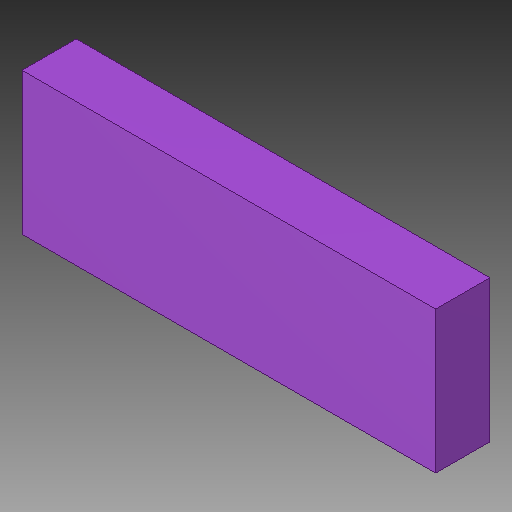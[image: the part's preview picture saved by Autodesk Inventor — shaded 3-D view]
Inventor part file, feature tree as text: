
AUTODESK INVENTOR PART (.ipt)
format: ipt  version: 2019 (Build 230136000, 136)  size: 88,064 bytes
history: native  units: in
note: dims shown in document units (in); Inventor stores cm internally (conversion verified against a paired STEP export)
features: extrude x1, other x1
ambient origin geometry x8: Origin, YZ Plane, XZ Plane, XY Plane, X Axis, Y Axis, Z Axis, Center Point
bodies: Solid1 (feature_tree)
feature tree (2):
  extrude  "Extrusion1"  Depth=0.0394in TaperAngle=0.0deg
  other  "1X03, SIGNALOUT_1X03_19"
